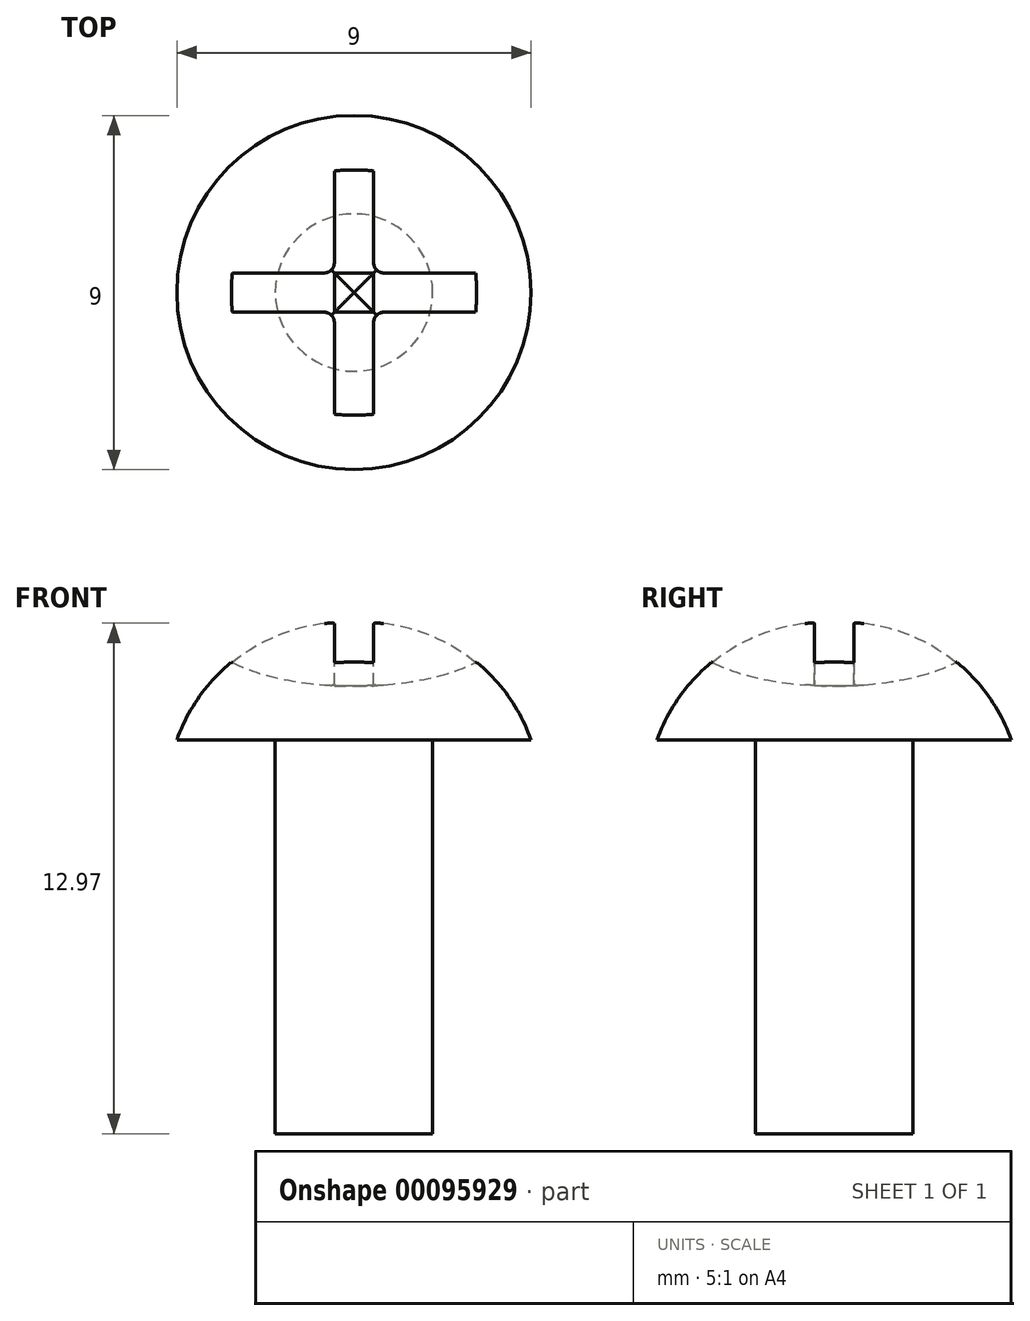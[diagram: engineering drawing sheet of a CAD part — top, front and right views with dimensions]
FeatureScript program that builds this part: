
annotation { "Feature Type Name" : "Feature", "Feature Type Description" : "" }
export const myFeature = defineFeature(function(context is Context, id is Id, definition is map)
    precondition{}
    {
        {
            var Q0;
            Q0=qCreatedBy(makeId("Front.planeOp"),FACE);
            var sketch = newSketch(context, id + "F0", { "sketchPlane" : qUnion([Q0])});
            skLineSegment(sketch, "E0", {"start": v(0, 0) * mm, "end": v(0, 3) * mm});
            skLineSegment(sketch, "E1", {"start": v(0, 0) * mm, "end": v(-4.5, 0) * mm});
            skPoint(sketch, "E2", {"position": v(0, 3) * mm});
            skPoint(sketch, "E3", {"position": v(-4.5, 0) * mm});
            skArc(sketch, "E4", {"start": v(0, 3) * mm, "mid": v(-2.75, 2.25) * mm, "end": v(-4.5, 0) * mm});
            skSolve(sketch);
        }
        {
            var Q0;
            Q0=makeQuery(id+"F0.imprint","IMPRINT",FACE,{"disambiguationData":[TD([[makeQuery(id+"F0.imprint","IMPRINT",EDGE,{"derivedFrom":sQuery(id+"F0.wireOp",EDGE,"E0")}),1.0]])]});
            var Q1;
            Q1=sQuery(id+"F0.wireOp",EDGE,"E0");
            revolve(context, id + "F1", {"entities" : qUnion([Q0]), "axis" : qUnion([Q1]), "revolveType" : RevolveType.FULL});
        }
        {
            var Q0;
            Q0=makeQuery(id+"F1.opRevolve","SWEPT_FACE",FACE,{"disambiguationData":[OSD([sQuery(id+"F0.wireOp",EDGE,"E1")])]});
            var sketch = newSketch(context, id + "F2", { "sketchPlane" : qUnion([Q0])});
            skCircle(sketch, "E5", {"center": v(0, 0) * mm, "radius": 2 * mm});
            skSolve(sketch);
        }
        {
            var Q0;
            Q0 = qSketchRegion(id + "F2", true);
            extrude(context, id + "F3", {"entities" : qUnion([Q0]), "operationType" : NewBodyOperationType.ADD, "depth" : 10 * mm});
        }
        {
            var Q0;
            Q0=qCreatedBy(makeId("Front.planeOp"),FACE);
            var sketch = newSketch(context, id + "F4", { "sketchPlane" : qUnion([Q0])});
            skEllipse(sketch, "E6", {"center": v(0, 3) * mm, "majorRadius": 4 * mm, "minorRadius": 1.63 * mm, "majorAxis": v(1, 0)});
            skSolve(sketch);
        }
        {
            var Q0;
            Q0 = qSketchRegion(id + "F4", true);
            extrude(context, id + "F5", {"entities" : qUnion([Q0]), "operationType" : NewBodyOperationType.REMOVE, "endBound" : BoundingType.SYMMETRIC, "depth" : 1 * mm});
        }
        {
            var Q0;
            Q0=qCreatedBy(makeId("Right.planeOp"),FACE);
            var sketch = newSketch(context, id + "F6", { "sketchPlane" : qUnion([Q0])});
            skEllipse(sketch, "E7", {"center": v(0, 3) * mm, "majorRadius": 4 * mm, "minorRadius": 1.63 * mm, "majorAxis": v(-1, 0)});
            skSolve(sketch);
        }
        {
            var Q0;
            Q0 = qSketchRegion(id + "F6", true);
            extrude(context, id + "F7", {"entities" : qUnion([Q0]), "operationType" : NewBodyOperationType.REMOVE, "endBound" : BoundingType.SYMMETRIC, "oppositeDirection" : true, "depth" : 1 * mm});
        }
        {
            var Q0;
            Q0=makeQuery(id+"F7.boolean.opBoolean","INTERSECT",EDGE,{"derivedFrom":[makeQuery(id+"F5.boolean.opBoolean","COPY",FACE,{"derivedFrom":makeQuery(id+"F5.opExtrude","CAP_FACE",FACE,{"disambiguationData":[OSD([sQuery(id+"F4.wireOp",EDGE,"E6")])],"isStart":true})}),makeQuery(id+"F7.opExtrude","CAP_FACE",FACE,{"disambiguationData":[OSD([sQuery(id+"F6.wireOp",EDGE,"E7")])],"isStart":true})]});
            var Q1;
            Q1=makeQuery(id+"F7.boolean.opBoolean","INTERSECT",EDGE,{"derivedFrom":[makeQuery(id+"F5.boolean.opBoolean","COPY",FACE,{"derivedFrom":makeQuery(id+"F5.opExtrude","CAP_FACE",FACE,{"disambiguationData":[OSD([sQuery(id+"F4.wireOp",EDGE,"E6")])],"isStart":false})}),makeQuery(id+"F7.opExtrude","CAP_FACE",FACE,{"disambiguationData":[OSD([sQuery(id+"F6.wireOp",EDGE,"E7")])],"isStart":true})]});
            var Q2;
            Q2=makeQuery(id+"F7.boolean.opBoolean","INTERSECT",EDGE,{"derivedFrom":[makeQuery(id+"F5.boolean.opBoolean","COPY",FACE,{"derivedFrom":makeQuery(id+"F5.opExtrude","CAP_FACE",FACE,{"disambiguationData":[OSD([sQuery(id+"F4.wireOp",EDGE,"E6")])],"isStart":true})}),makeQuery(id+"F7.opExtrude","CAP_FACE",FACE,{"disambiguationData":[OSD([sQuery(id+"F6.wireOp",EDGE,"E7")])],"isStart":false})]});
            var Q3;
            Q3=makeQuery(id+"F7.boolean.opBoolean","INTERSECT",EDGE,{"derivedFrom":[makeQuery(id+"F5.boolean.opBoolean","COPY",FACE,{"derivedFrom":makeQuery(id+"F5.opExtrude","CAP_FACE",FACE,{"disambiguationData":[OSD([sQuery(id+"F4.wireOp",EDGE,"E6")])],"isStart":false})}),makeQuery(id+"F7.opExtrude","CAP_FACE",FACE,{"disambiguationData":[OSD([sQuery(id+"F6.wireOp",EDGE,"E7")])],"isStart":false})]});
            fillet(context, id + "F8", {"entities" : qUnion([Q0, Q1, Q2, Q3]), "radius" : .25 * mm, "tangentPropagation" : true, "allowEdgeOverflow" : false});
        }
    });
